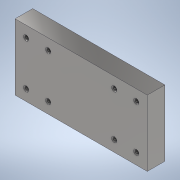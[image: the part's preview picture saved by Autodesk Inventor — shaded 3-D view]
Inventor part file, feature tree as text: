
AUTODESK INVENTOR PART (.ipt)
format: ipt  version: 2021 (Build 250183000, 183)  size: 148,480 bytes
history: native  units: mm
features: extrude x2, sketch x2, other x1, chamfer x1
ambient origin geometry x8: Origin, YZ Plane, XZ Plane, XY Plane, X Axis, Y Axis, Z Axis, Center Point
bodies: Body1 (feature_tree)
feature tree (6):
  other  "Sólido1"
  extrude  "Extrusão1"  Depth=300.0mm
  extrude  "Extrusão2"  Depth=40.0mm
  chamfer  "Chanfro1"  Distance=200.0mm
  sketch  "Esboço1"  dims[d0=600.0mm d1=300.0mm]
  sketch  "Esboço2"  dims[d2=80.0mm d3=0.0mm d4=500.0mm d5=200.0mm d6=300.0mm d7=16.0mm d8=16.0mm d9=16.0mm d10=16.0mm d11=16.0mm d12=16.0mm d13=16.0mm d14=16.0mm d15=40.0mm d16=0.0mm d17=4.0mm d18=2.0mm d19=45.0deg]
